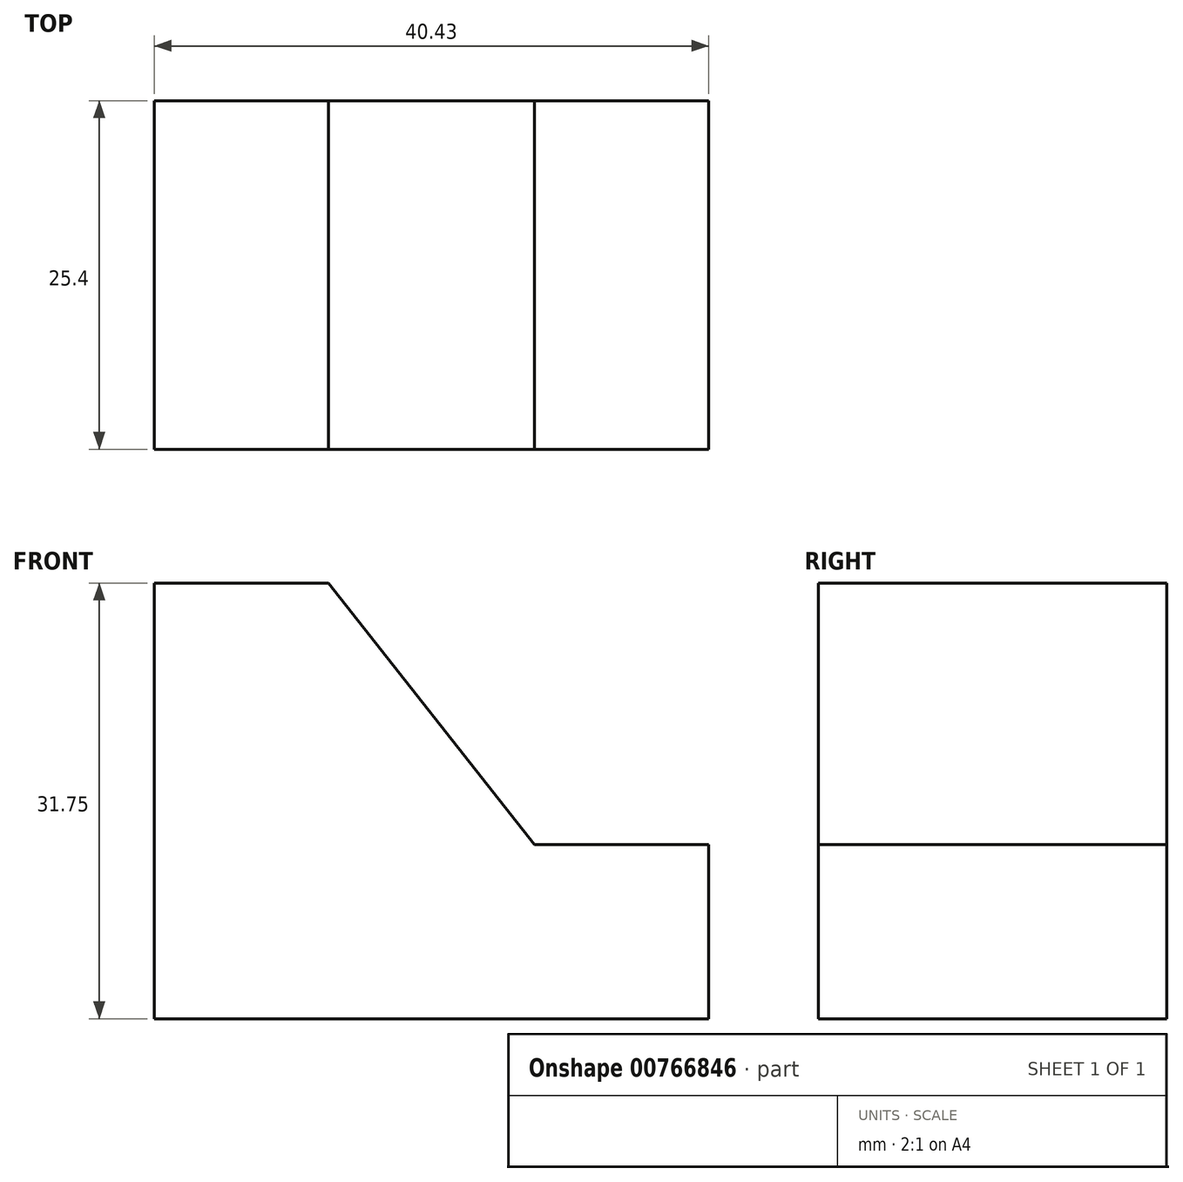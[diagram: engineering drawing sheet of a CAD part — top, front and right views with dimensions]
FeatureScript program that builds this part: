
annotation { "Feature Type Name" : "Feature", "Feature Type Description" : "" }
export const myFeature = defineFeature(function(context is Context, id is Id, definition is map)
    precondition{}
    {
        {
            var Q0;
            Q0=qCreatedBy(makeId("Front.planeOp"),FACE);
            var sketch = newSketch(context, id + "F0", { "sketchPlane" : qUnion([Q0])});
            skLineSegment(sketch, "E0", {"start": v(2.33, 0) * mm, "end": v(40.43, 0) * mm});
            skLineSegment(sketch, "E1", {"start": v(40.43, 0) * mm, "end": v(0, 0) * mm});
            skLineSegment(sketch, "E2", {"start": v(0, 0) * mm, "end": v(0, 31.75) * mm});
            skLineSegment(sketch, "E3", {"start": v(40.43, 0) * mm, "end": v(40.43, 12.7) * mm});
            skLineSegment(sketch, "E4", {"start": v(40.43, 12.7) * mm, "end": v(27.73, 12.7) * mm});
            skLineSegment(sketch, "E5", {"start": v(0, 31.75) * mm, "end": v(12.7, 31.75) * mm});
            skLineSegment(sketch, "E6", {"start": v(12.7, 31.75) * mm, "end": v(27.73, 12.7) * mm});
            skSolve(sketch);
        }
        {
            var Q0;
            {var subQ1=sQuery(id+"F0.wireOp",EDGE,"E2");Q0=makeQuery(id+"F0.imprint","IMPRINT",FACE,{"disambiguationData":[TD([[makeQuery(id+"F0.imprint","IMPRINT",EDGE,{"derivedFrom":subQ1}),-1.0]])]});}
            extrude(context, id + "F1", {"entities" : qUnion([Q0]), "depth" : 25.4 * mm, "offsetDistance" : 25.4 * mm});
        }
    });
